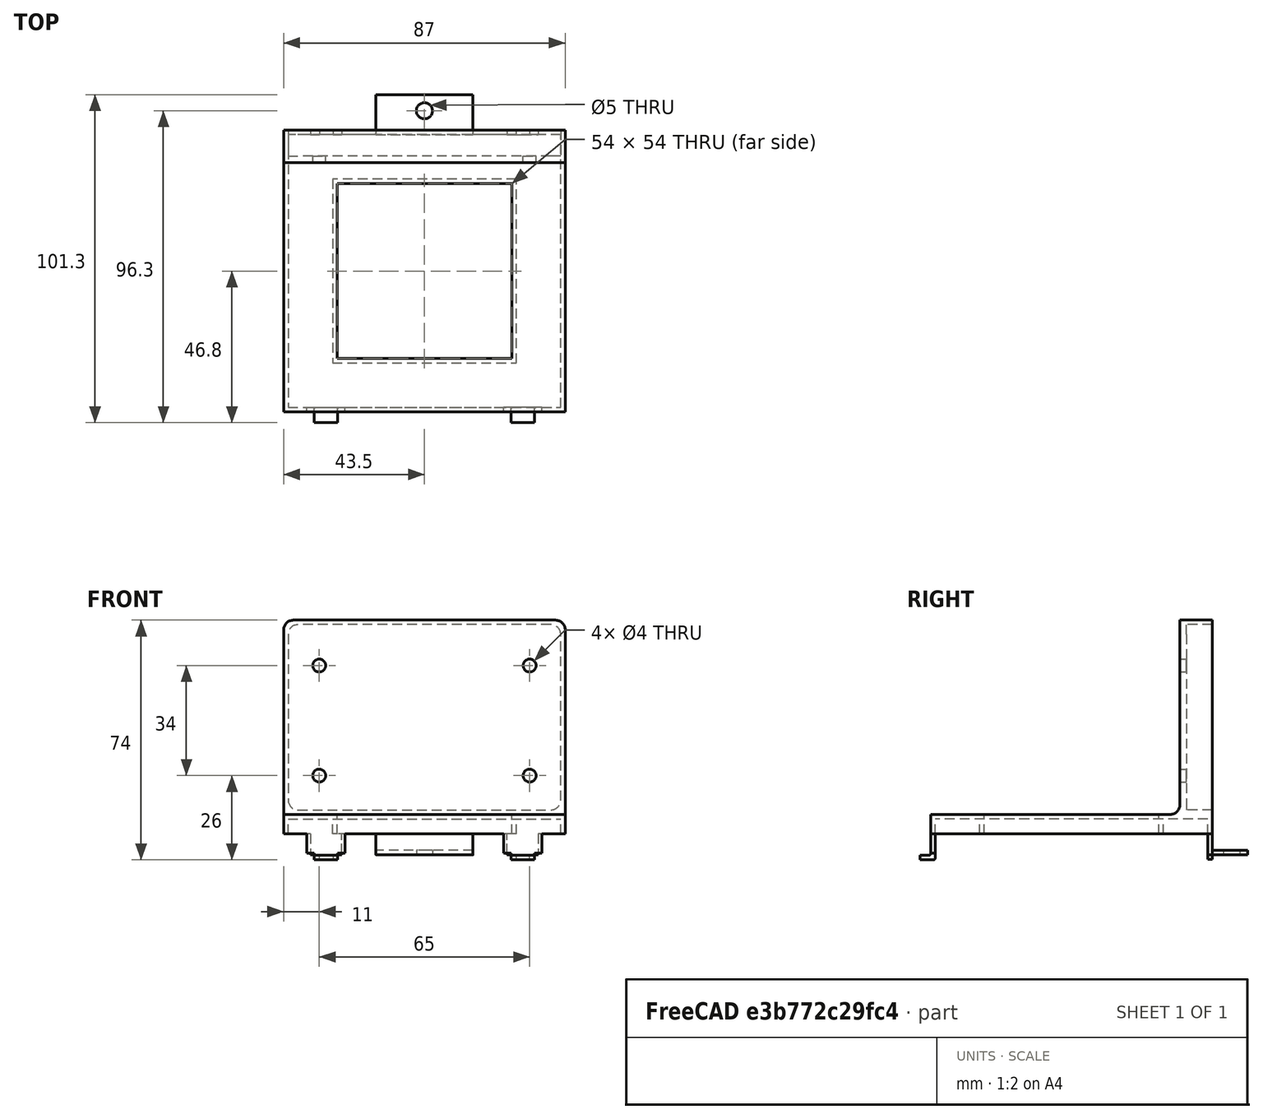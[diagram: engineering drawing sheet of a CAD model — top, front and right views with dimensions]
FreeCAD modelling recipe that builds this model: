
FCSTD DOCUMENT  (FreeCAD 0.21R33668 +7 (Git))
Label: TheTower900Adapter
License: All rights reserved
LicenseURL: http://austrianinstruments.at/All_rights_reserved
objects: TechDraw::DrawViewDimension×24, Sketcher::SketchObject×11, PartDesign::Pad×7, PartDesign::Plane×3, TechDraw::DrawProjGroupItem×3, PartDesign::Pocket×2, TechDraw::DrawSVGTemplate×2, PartDesign::Hole×2, PartDesign::Fillet×2, TechDraw::DrawPage×2, Spreadsheet::Sheet×1, TechDraw::DrawViewSymbol×1, PartDesign::Mirrored×1, PartDesign::Body×1, TechDraw::DrawProjGroup×1, TechDraw::DrawViewDetail×1, TechDraw::DrawViewPart×1
note: 50 computed .brp shape members not serialized (recipe doc carries the construction recipe); baked Part::Feature solids carry a one-line shape summary decoded from their .brp

FEATURE [Sketcher::SketchObject] Sketch
  FullyConstrained = true
  MapMode = 5
  Support = -> [XY_Plane]
  expr: Constraints[20] = Spreadsheet.mainbodywidth
  expr: Constraints[21] = Spreadsheet.mainbodyholewidth
  sketch-geometry (10):
    g0: LineSegment StartX=-43.5 StartY=43.5 StartZ=0 EndX=-43.5 EndY=-43.5 EndZ=0
    g1: LineSegment StartX=-43.5 StartY=-43.5 StartZ=0 EndX=43.5 EndY=-43.5 EndZ=0
    g2: LineSegment StartX=43.5 StartY=-43.5 StartZ=0 EndX=43.5 EndY=43.5 EndZ=0
    g3: LineSegment StartX=43.5 StartY=43.5 StartZ=0 EndX=-43.5 EndY=43.5 EndZ=0
    g4: GeomPoint X=0 Y=0 Z=0
    g5: LineSegment StartX=-27 StartY=27 StartZ=0 EndX=-27 EndY=-27 EndZ=0
    g6: LineSegment StartX=-27 StartY=-27 StartZ=0 EndX=27 EndY=-27 EndZ=0
    g7: LineSegment StartX=27 StartY=-27 StartZ=0 EndX=27 EndY=27 EndZ=0
    g8: LineSegment StartX=27 StartY=27 StartZ=0 EndX=-27 EndY=27 EndZ=0
    g9: GeomPoint X=0 Y=0 Z=0
  constraints (24):
    c: Coincident(g0,g1)
    c: Coincident(g1,g2)
    c: Coincident(g2,g3)
    c: Coincident(g3,g0)
    c: Horizontal(g1)
    c: Horizontal(g3)
    c: Vertical(g0)
    c: Vertical(g2)
    c: Symmetric(g1,g0,g4)
    c: Coincident(g4,g-1)
    c: Coincident(g5,g6)
    c: Coincident(g6,g7)
    c: Coincident(g7,g8)
    c: Coincident(g8,g5)
    c: Horizontal(g6)
    c: Horizontal(g8)
    c: Vertical(g5)
    c: Vertical(g7)
    c: Symmetric(g6,g5,g9)
    c: Coincident(g9,g4)
    c: DistanceY(g0,g0) = 87
    c: DistanceY(g5,g5) = 54
    c: Equal(g8,g5)
    c: Equal(g3,g0)
FEATURE [PartDesign::Pad] Pad  label="Main body"
  Direction = (0,0,1)
  Length = 6
  Length2 = 10
  Profile = -> Sketch
  ReferenceAxis = -> Sketch [N_Axis]
  Type = 0
  expr: Length = Spreadsheet.mainbodyheight
FEATURE [Sketcher::SketchObject] Sketch001
  FullyConstrained = true
  MapMode = 5
  Support = -> [XY_Plane]
  expr: Constraints[11] = Spreadsheet.mainbodywidth - Spreadsheet.mainbodywallthickness * 2
  expr: Constraints[22] = Spreadsheet.mainbodyholewidth + Spreadsheet.mainbodywallthickness * 2
  sketch-geometry (10):
    g0: LineSegment StartX=-42.1 StartY=42.1 StartZ=0 EndX=-42.1 EndY=-42.1 EndZ=0
    g1: LineSegment StartX=-42.1 StartY=-42.1 StartZ=0 EndX=42.1 EndY=-42.1 EndZ=0
    g2: LineSegment StartX=42.1 StartY=-42.1 StartZ=0 EndX=42.1 EndY=42.1 EndZ=0
    g3: LineSegment StartX=42.1 StartY=42.1 StartZ=0 EndX=-42.1 EndY=42.1 EndZ=0
    g4: GeomPoint X=0 Y=0 Z=0
    g5: LineSegment StartX=-28.4 StartY=28.4 StartZ=0 EndX=-28.4 EndY=-28.4 EndZ=0
    g6: LineSegment StartX=-28.4 StartY=-28.4 StartZ=0 EndX=28.4 EndY=-28.4 EndZ=0
    g7: LineSegment StartX=28.4 StartY=-28.4 StartZ=0 EndX=28.4 EndY=28.4 EndZ=0
    g8: LineSegment StartX=28.4 StartY=28.4 StartZ=0 EndX=-28.4 EndY=28.4 EndZ=0
    g9: GeomPoint X=0 Y=0 Z=0
  constraints (24):
    c: Coincident(g0,g1)
    c: Coincident(g1,g2)
    c: Coincident(g2,g3)
    c: Coincident(g3,g0)
    c: Horizontal(g1)
    c: Horizontal(g3)
    c: Vertical(g0)
    c: Vertical(g2)
    c: Symmetric(g1,g0,g4)
    c: Coincident(g4,g-1)
    c: Equal(g3,g2)
    c: DistanceY(g0,g0) = 84.2
    c: Coincident(g5,g6)
    c: Coincident(g6,g7)
    c: Coincident(g7,g8)
    c: Coincident(g8,g5)
    c: Horizontal(g6)
    c: Horizontal(g8)
    c: Vertical(g5)
    c: Vertical(g7)
    c: Symmetric(g6,g5,g9)
    c: Coincident(g9,g4)
    c: DistanceY(g5,g5) = 56.8
    c: Equal(g5,g8)
FEATURE [PartDesign::Pocket] Pocket  label="Main body pocket"
  BaseFeature = -> Pad
  Direction = (0,0,-1)
  Length = 4.6
  Length2 = 5
  Profile = -> Sketch001
  ReferenceAxis = -> Sketch001 [N_Axis]
  Reversed = true
  Type = 0
  expr: Length = Spreadsheet.mainbodypocketdepth
FEATURE [PartDesign::Plane] DatumPlane  label="Front fixture reference plane"
  AttachmentOffset = pos=(0,0,43.5) rot=(0,0,1;0rad)
  Length = 60
  MapMode = 3
  Placement = pos=(0,-43.5,9.7e-15) rot=(1,0,0;1.5708rad)
  ResizeMode = 0
  Support = -> [XY_Plane]
  Width = 60
  expr: .AttachmentOffset.Base.z = Spreadsheet.mainbodywidth / 2
FEATURE [Sketcher::SketchObject] Sketch002
  FullyConstrained = true
  MapMode = 5
  Placement = pos=(0,-43.5,9.7e-15) rot=(1,0,0;1.5708rad)
  Support = -> [DatumPlane]
  expr: Constraints[18] = Spreadsheet.frontfixturewidth1
  expr: Constraints[19] = Spreadsheet.frontfixtureheight1
  expr: Constraints[21] = Spreadsheet.frontfixturewidth2
  expr: Constraints[22] = Spreadsheet.frontfixturedistance / 2
  expr: Constraints[23] = Spreadsheet.frontfixtureheight2
  sketch-geometry (8):
    g0: LineSegment StartX=-36.3 StartY=0 StartZ=0 EndX=-24.5 EndY=0 EndZ=0
    g1: LineSegment StartX=-24.5 StartY=0 StartZ=0 EndX=-24.5 EndY=-6 EndZ=0
    g2: LineSegment StartX=-36.3 StartY=-6 StartZ=0 EndX=-36.3 EndY=0 EndZ=0
    g3: LineSegment StartX=-36.3 StartY=-6 StartZ=0 EndX=-34.025 EndY=-6 EndZ=0
    g4: LineSegment StartX=-34.025 StartY=-6 StartZ=0 EndX=-34.025 EndY=-8 EndZ=0
    g5: LineSegment StartX=-34.025 StartY=-8 StartZ=0 EndX=-26.775 EndY=-8 EndZ=0
    g6: LineSegment StartX=-26.775 StartY=-8 StartZ=0 EndX=-26.775 EndY=-6 EndZ=0
    g7: LineSegment StartX=-26.775 StartY=-6 StartZ=0 EndX=-24.5 EndY=-6 EndZ=0
  constraints (24):
    c: Coincident(g0,g1)
    c: Coincident(g2,g0)
    c: Horizontal(g0)
    c: Vertical(g1)
    c: Vertical(g2)
    c: PointOnObject(g0,g-1)
    c: Coincident(g3,g2)
    c: Horizontal(g3)
    c: Coincident(g4,g3)
    c: Vertical(g4)
    c: Coincident(g5,g4)
    c: Horizontal(g5)
    c: Coincident(g6,g5)
    c: Vertical(g6)
    c: Coincident(g7,g6)
    c: Coincident(g7,g1)
    c: Horizontal(g7)
    c: Equal(g3,g7)
    c: DistanceX(g0,g0) = 11.8
    c: DistanceY(g2,g2) = 6
    c: Horizontal(g3,g6)
    c: DistanceX(g5,g5) = 7.25
    c: DistanceX(g0,g-1) = 24.5
    c: DistanceY(g4,g2) = 2
FEATURE [PartDesign::Pad] Pad001  label="Front fixture vertical part"
  BaseFeature = -> Pocket
  Direction = (0,-1,2e-16)
  Length = 1.4
  Length2 = 10
  Profile = -> Sketch002
  ReferenceAxis = -> Sketch002 [N_Axis]
  Reversed = true
  Type = 0
  expr: Length = Spreadsheet.mainbodywallthickness
FEATURE [Sketcher::SketchObject] Sketch003
  FullyConstrained = true
  MapMode = 5
  Placement = pos=(0,-43.5,9.7e-15) rot=(1,0,0;1.5708rad)
  Support = -> [DatumPlane]
  expr: Constraints[10] = Spreadsheet.frontfixturedistance / 2 + (Spreadsheet.frontfixturewidth1 - Spreadsheet.frontfixturewidth2) / 2
  expr: Constraints[11] = Spreadsheet.frontfixtureheight1 + Spreadsheet.frontfixtureheight2
  expr: Constraints[7] = Spreadsheet.mainbodywallthickness
  expr: Constraints[9] = Spreadsheet.frontfixturewidth2
  sketch-geometry (4):
    g0: LineSegment StartX=-34.025 StartY=-6.6 StartZ=0 EndX=-26.775 EndY=-6.6 EndZ=0
    g1: LineSegment StartX=-26.775 StartY=-6.6 StartZ=0 EndX=-26.775 EndY=-8 EndZ=0
    g2: LineSegment StartX=-26.775 StartY=-8 StartZ=0 EndX=-34.025 EndY=-8 EndZ=0
    g3: LineSegment StartX=-34.025 StartY=-8 StartZ=0 EndX=-34.025 EndY=-6.6 EndZ=0
  constraints (12):
    c: Horizontal(g0)
    c: Vertical(g1)
    c: Vertical(g3)
    c: Coincident(g1,g2)
    c: Coincident(g2,g3)
    c: Coincident(g0,g3)
    c: Coincident(g0,g1)
    c: DistanceY(g3,g3) = 1.4
    c: Horizontal(g2)
    c: DistanceX(g0,g0) = 7.25
    c: DistanceX(g0,g-1) = 26.775
    c: DistanceY(g1,g-1) = 8
FEATURE [PartDesign::Pad] Pad002  label="Front fixture horizontal part"
  BaseFeature = -> Pad001
  Direction = (0,-1,2e-16)
  Length = 3.3
  Length2 = 10
  Profile = -> Sketch003
  ReferenceAxis = -> Sketch003 [N_Axis]
  Type = 0
  expr: Length = Spreadsheet.frontfixturehorizontalpartlength
FEATURE [Spreadsheet::Sheet] Spreadsheet
  cells = A1='mainbodywidth; B1(mainbodywidth)=87; A2='mainbodyholewidth; B2(mainbodyholewidth)=54; A3='mainbodyheight; B3(mainbodyheight)=6; A4='mainbodywallthickness; B4(mainbodywallthickness)=1.4; A5='mainbodypocketdepth; B5(mainbodypocketdepth)==mainbodyheight - mainbodywallthickness; A6='frontfixturedistance; B6(frontfixturedistance)=49; A7='frontfixturewidth1; B7(frontfixturewidth1)=11.8; A8='frontfixturewidth2; B8(frontfixturewidth2)=7.25; A9='frontfixtureheight1; B9(frontfixtureheight1)==12 - mainbodyheight; A10='frontfixtureheight2; B10(frontfixtureheight2)==14 - mainbodyheight - frontfixtureheight1; A11='frontfixturehorizontalpartlength; B11(frontfixturehorizontalpartlength)=3.3; A12='backfixturedistance; B12(backfixturedistance)=51; A13='backfixturewidth1; B13(backfixturewidth1)=9.7; A14='backfixturewidth2; B14(backfixturewidth2)=4.2; A15='backfixtureheight1; B15(backfixtureheight1)==12.5 - mainbodyheight; A16='backfixtureheight2; B16(backfixtureheight2)==13.85 - backfixtureheight1 - mainbodyheight; A17='floorfixtureverticalwidth; B17(floorfixtureverticalwidth)=30; A18='floorfixturehorizontalpartheight; B18(floorfixturehorizontalpartheight)==mainbodywallthickness; A19='floorfixturehorizontalparthlength; B19(floorfixturehorizontalparthlength)=11; A20='socketlength; B20(socketlength)=10; A21='socketheight; B21(socketheight)=60; A22='socketholeshorizontaldistance; B22(socketholeshorizontaldistance)=65; A23='socketholesverticaldistance; B23(socketholesverticaldistance)=34; A24='socketholescenterheight; B24(socketholescenterheight)=35; A25='socketholesradius; B25(socketholesradius)=2
FEATURE [PartDesign::Plane] DatumPlane001  label="Back fixture reference plane"
  AttachmentOffset = pos=(0,0,-43.5) rot=(0,0,1;0rad)
  Length = 60
  MapMode = 5
  Placement = pos=(0,43.5,9.7e-15) rot=(1,0,0;1.5708rad)
  ResizeMode = 0
  Support = -> [XZ_Plane]
  Width = 60
  expr: .AttachmentOffset.Base.z = -Spreadsheet.mainbodywidth / 2
FEATURE [Sketcher::SketchObject] Sketch004
  FullyConstrained = true
  MapMode = 5
  Placement = pos=(0,43.5,9.7e-15) rot=(1,0,0;1.5708rad)
  Support = -> [DatumPlane001]
  expr: Constraints[10] = Spreadsheet.backfixtureheight1
  expr: Constraints[8] = Spreadsheet.floorfixtureverticalwidth
  sketch-geometry (4):
    g0: LineSegment StartX=-15 StartY=0 StartZ=0 EndX=15 EndY=0 EndZ=0
    g1: LineSegment StartX=15 StartY=0 StartZ=0 EndX=15 EndY=-6.5 EndZ=0
    g2: LineSegment StartX=15 StartY=-6.5 StartZ=0 EndX=-15 EndY=-6.5 EndZ=0
    g3: LineSegment StartX=-15 StartY=-6.5 StartZ=0 EndX=-15 EndY=0 EndZ=0
  constraints (11):
    c: Coincident(g0,g1)
    c: Coincident(g1,g2)
    c: Coincident(g2,g3)
    c: Coincident(g3,g0)
    c: Horizontal(g0)
    c: Horizontal(g2)
    c: Vertical(g1)
    c: Vertical(g3)
    c: DistanceX(g2,g2) = 30
    c: Symmetric(g0,g0,g-1)
    c: DistanceY(g3,g3) = 6.5
FEATURE [PartDesign::Plane] DatumPlane002  label="top reference plane"
  AttachmentOffset = pos=(0,0,6) rot=(0,0,1;0rad)
  Length = 60
  MapMode = 5
  Placement = pos=(0,0,6) rot=(0,0,1;0rad)
  ResizeMode = 0
  Support = -> [XY_Plane]
  Width = 60
FEATURE [Sketcher::SketchObject] Sketch006
  FullyConstrained = true
  MapMode = 5
  Placement = pos=(0,0,6) rot=(0,0,1;0rad)
  Support = -> [DatumPlane002]
  expr: Constraints[10] = Spreadsheet.mainbodywidth
  expr: Constraints[11] = Spreadsheet.mainbodywidth / 2
  expr: Constraints[12] = Spreadsheet.socketlength
  sketch-geometry (5):
    g0: LineSegment StartX=-43.5 StartY=43.5 StartZ=0 EndX=-43.5 EndY=33.5 EndZ=0
    g1: LineSegment StartX=-43.5 StartY=33.5 StartZ=0 EndX=43.5 EndY=33.5 EndZ=0
    g2: LineSegment StartX=43.5 StartY=33.5 StartZ=0 EndX=43.5 EndY=43.5 EndZ=0
    g3: LineSegment StartX=43.5 StartY=43.5 StartZ=0 EndX=-43.5 EndY=43.5 EndZ=0
    g4: GeomPoint X=0 Y=38.5 Z=0
  constraints (13):
    c: Coincident(g0,g1)
    c: Coincident(g1,g2)
    c: Coincident(g2,g3)
    c: Coincident(g3,g0)
    c: Horizontal(g1)
    c: Horizontal(g3)
    c: Vertical(g0)
    c: Vertical(g2)
    c: Symmetric(g1,g0,g4)
    c: PointOnObject(g4,g-2)
    c: DistanceX(g3,g3) = 87
    c: DistanceY(g-1,g0) = 43.5
    c: DistanceY(g0,g0) = 10
FEATURE [Sketcher::SketchObject] Sketch007
  FullyConstrained = true
  MapMode = 5
  Placement = pos=(0,0,0) rot=(1,0,0;1.5708rad)
  Support = -> [XZ_Plane]
  expr: Constraints[12] = Spreadsheet.socketholescenterheight
  expr: Constraints[7] = Spreadsheet.socketholesradius
  expr: Constraints[8] = Spreadsheet.socketholeshorizontaldistance
  expr: Constraints[9] = Spreadsheet.socketholesverticaldistance
  sketch-geometry (5):
    g0: Circle CenterX=-32.5 CenterY=52 CenterZ=0 NormalX=0 NormalY=0 NormalZ=1 AngleXU=0 Radius=2
    g1: Circle CenterX=32.5 CenterY=52 CenterZ=0 NormalX=0 NormalY=0 NormalZ=1 AngleXU=0 Radius=2
    g2: Circle CenterX=-32.5 CenterY=18 CenterZ=0 NormalX=0 NormalY=0 NormalZ=1 AngleXU=0 Radius=2
    g3: Circle CenterX=32.5 CenterY=18 CenterZ=0 NormalX=0 NormalY=0 NormalZ=1 AngleXU=0 Radius=2
    g4: GeomPoint X=0 Y=35 Z=0
  constraints (13):
    c: Vertical(g1,g3)
    c: Vertical(g0,g2)
    c: Horizontal(g0,g1)
    c: Horizontal(g2,g3)
    c: Equal(g0,g1)
    c: Equal(g1,g3)
    c: Equal(g3,g2)
    c: Radius(g0) = 2
    c: DistanceX(g0,g1) = 65
    c: DistanceY(g2,g0) = 34
    c: PointOnObject(g4,g-2)
    c: Symmetric(g0,g3,g4)
    c: DistanceY(g-1,g4) = 35
FEATURE [Sketcher::SketchObject] Sketch005
  FullyConstrained = true
  MapMode = 5
  Placement = pos=(0,43.5,9.7e-15) rot=(1,0,0;1.5708rad)
  Support = -> [DatumPlane001]
  expr: Constraints[10] = Spreadsheet.floorfixtureverticalwidth
  expr: Constraints[11] = Spreadsheet.backfixtureheight1
  expr: Constraints[12] = Spreadsheet.mainbodywallthickness
  sketch-geometry (5):
    g0: LineSegment StartX=-15 StartY=-5.1 StartZ=0 EndX=-15 EndY=-6.5 EndZ=0
    g1: LineSegment StartX=-15 StartY=-6.5 StartZ=0 EndX=15 EndY=-6.5 EndZ=0
    g2: LineSegment StartX=15 StartY=-6.5 StartZ=0 EndX=15 EndY=-5.1 EndZ=0
    g3: LineSegment StartX=15 StartY=-5.1 StartZ=0 EndX=-15 EndY=-5.1 EndZ=0
    g4: GeomPoint X=0 Y=-5.8 Z=0
  constraints (13):
    c: Coincident(g0,g1)
    c: Coincident(g1,g2)
    c: Coincident(g2,g3)
    c: Coincident(g3,g0)
    c: Horizontal(g1)
    c: Horizontal(g3)
    c: Vertical(g0)
    c: Vertical(g2)
    c: Symmetric(g1,g0,g4)
    c: PointOnObject(g4,g-2)
    c: DistanceX(g1,g1) = 30
    c: DistanceY(g0,g-1) = 6.5
    c: DistanceY(g0,g0) = 1.4
FEATURE [Sketcher::SketchObject] Sketch008
  FullyConstrained = true
  MapMode = 5
  Support = -> [XY_Plane]
  expr: Constraints[2] = Spreadsheet.mainbodywidth / 2 + Spreadsheet.floorfixturehorizontalparthlength - 5
  sketch-geometry (1):
    g0: Circle CenterX=0 CenterY=49.5 CenterZ=0 NormalX=0 NormalY=0 NormalZ=1 AngleXU=0 Radius=2.5
  constraints (3):
    c: PointOnObject(g0,g-2)
    c: Radius(g0) = 2.5
    c: DistanceY(g-1,g0) = 49.5
FEATURE [Sketcher::SketchObject] Sketch009
  FullyConstrained = true
  MapMode = 5
  Placement = pos=(0,43.5,9.7e-15) rot=(1,0,0;1.5708rad)
  Support = -> [DatumPlane001]
  expr: Constraints[10] = Spreadsheet.mainbodyheight + Spreadsheet.socketheight / 2
  expr: Constraints[11] = Spreadsheet.mainbodywidth - Spreadsheet.mainbodywallthickness * 2
  expr: Constraints[12] = Spreadsheet.socketheight - Spreadsheet.mainbodywallthickness * 2
  sketch-geometry (5):
    g0: LineSegment StartX=-42.1 StartY=64.6 StartZ=0 EndX=-42.1 EndY=7.4 EndZ=0
    g1: LineSegment StartX=-42.1 StartY=7.4 StartZ=0 EndX=42.1 EndY=7.4 EndZ=0
    g2: LineSegment StartX=42.1 StartY=7.4 StartZ=0 EndX=42.1 EndY=64.6 EndZ=0
    g3: LineSegment StartX=42.1 StartY=64.6 StartZ=0 EndX=-42.1 EndY=64.6 EndZ=0
    g4: GeomPoint X=1e-16 Y=36 Z=0
  constraints (13):
    c: Coincident(g0,g1)
    c: Coincident(g1,g2)
    c: Coincident(g2,g3)
    c: Coincident(g3,g0)
    c: Horizontal(g1)
    c: Horizontal(g3)
    c: Vertical(g0)
    c: Vertical(g2)
    c: Symmetric(g1,g0,g4)
    c: PointOnObject(g4,g-2)
    c: DistanceY(g-1,g4) = 36
    c: DistanceX(g3,g3) = 84.2
    c: DistanceY(g2,g2) = 57.2
FEATURE [TechDraw::DrawSVGTemplate] Template
  EditableTexts = APPROVER_NAME=Equilibrium; AUTHOR_NAME=Equilibrium; DATE=2023-09-01; DN=1; DOCUMENT_TYPE=Mechanical assembly drawing; OWNER_NAME=Equilibrium; PM=Plastic; PN=1; REVISION=REV 1; RIGHTS=Can be distributed without permission; SCALE=M x:x; SHEET=1 of 1; SIZE=A3; TITLELINE-1=Adapter for PC Waterpump; TITLELINE-2=EK-Quantum Kinetic TBE 300 D5 PWM D-RGB; TITLELINE-3=for The Tower 900 Chassis; TOLERANCE=+/- ?
  Height = 297
  Orientation = 1
  Width = 420
FEATURE [TechDraw::DrawSVGTemplate] Template001
  EditableTexts = APPROVER_NAME=Equilibrium; AUTHOR_NAME=Equilibrium; DATE=2023-09-01; DN=1; DOCUMENT_TYPE=Mechanical assembly drawing; OWNER_NAME=Equilibrium; PM=Plastic; PN=1; REVISION=REV 1; RIGHTS=(R) DO NOT DUPLICATE THIS DRAWING TO THIRD PARTIES WITHOUT OWNER'S PERMISSION!; SCALE=M x:x; SHEET=1 of 1; SIZE=A3; TITLELINE-1=Adapter for PC Waterpump; TITLELINE-2=EK-Quantum Kinetic TBE 300 D5 PWM D-RGB; TITLELINE-3=for The Tower 900 Chassis; TOLERANCE=+/- ?
  Height = 297
  Orientation = 1
  Width = 420
FEATURE [TechDraw::DrawViewSymbol] SurfaceSymbol
  LockPosition = false
  Rotation = 0
  ScaleType = 2
  Symbol = <?xml version='1.0'?>\n<svg width='150' height='64'>\n<path stroke='#000' stroke-width='1' d=' M0, 44 L12, 64' />\n<path stroke='#000' stroke-width='1' d=' M12, 64 L42, 14' />\n<circle cx='12' cy='46' r='9' fill='none' stroke='#000' stroke-width='1'/>\n<text x='42' y='11' style='font-size:18px'>3D Print</text>\n<text x='42' y='30' style='font-size:18px'>Ra50</text>\n<path stroke='#000' stroke-width='1' d=' M42, 14 L116, 14' />\n<text x='20' y='60' style='font-size:18px'></text>\n<text x='-25' y='60' style='font-size:18px'></text>\n</svg>
  X = 155
  Y = 275.5
FEATURE [Sketcher::SketchObject] Sketch010
  FullyConstrained = true
  MapMode = 5
  Placement = pos=(0,43.5,9.7e-15) rot=(1,0,0;1.5708rad)
  Support = -> [DatumPlane001]
  expr: Constraints[20] = Spreadsheet.backfixturewidth2
  expr: Constraints[21] = Spreadsheet.backfixturedistance / 2
  expr: Constraints[22] = Spreadsheet.backfixtureheight1
  expr: Constraints[23] = Spreadsheet.backfixtureheight2
  expr: Constraints[9] = Spreadsheet.backfixturewidth1
  sketch-geometry (8):
    g0: LineSegment StartX=-25.5 StartY=0 StartZ=0 EndX=-35.2 EndY=0 EndZ=0
    g1: LineSegment StartX=-35.2 StartY=0 StartZ=0 EndX=-35.2 EndY=-6.5 EndZ=0
    g2: LineSegment StartX=-35.2 StartY=-6.5 StartZ=0 EndX=-32.45 EndY=-6.5 EndZ=0
    g3: LineSegment StartX=-25.5 StartY=-6.5 StartZ=0 EndX=-25.5 EndY=0 EndZ=0
    g4: LineSegment StartX=-28.25 StartY=-6.5 StartZ=0 EndX=-28.25 EndY=-7.85 EndZ=0
    g5: LineSegment StartX=-28.25 StartY=-7.85 StartZ=0 EndX=-32.45 EndY=-7.85 EndZ=0
    g6: LineSegment StartX=-32.45 StartY=-7.85 StartZ=0 EndX=-32.45 EndY=-6.5 EndZ=0
    g7: LineSegment StartX=-28.25 StartY=-6.5 StartZ=0 EndX=-25.5 EndY=-6.5 EndZ=0
  constraints (24):
    c: Coincident(g0,g1)
    c: Coincident(g1,g2)
    c: Coincident(g7,g3)
    c: Coincident(g3,g0)
    c: Horizontal(g0)
    c: Horizontal(g2)
    c: Vertical(g1)
    c: Vertical(g3)
    c: PointOnObject(g0,g-1)
    c: DistanceX(g0,g0) = 9.7
    c: Coincident(g5,g4)
    c: Horizontal(g5)
    c: Coincident(g6,g5)
    c: Coincident(g2,g6)
    c: Coincident(g7,g4)
    c: Equal(g7,g2)
    c: Equal(g3,g1)
    c: Vertical(g4)
    c: Vertical(g6)
    c: Horizontal(g7)
    c: DistanceX(g5,g5) = 4.2
    c: DistanceX(g0,g-1) = 25.5
    c: DistanceY(g1,g1) = 6.5
    c: DistanceY(g5,g1) = 1.35
FEATURE [PartDesign::Pad] Pad006  label="Back fixture vertical part"
  BaseFeature = -> Pad002
  Direction = (0,-1,-2e-16)
  Length = 1.4
  Length2 = 10
  Profile = -> Sketch010
  ReferenceAxis = -> Sketch010 [N_Axis]
  Type = 0
  expr: Length = Spreadsheet.mainbodywallthickness
FEATURE [PartDesign::Mirrored] Mirrored002  label="Fixture mirroring"
  BaseFeature = -> Pad006
  MirrorPlane = -> Sketch003 [V_Axis]
  Originals = -> [Pad001,Pad002,Pad006]
FEATURE [PartDesign::Pad] Pad003  label="Floor fixture vertical"
  BaseFeature = -> Mirrored002
  Direction = (0,-1,-2e-16)
  Length = 1.4
  Length2 = 10
  Profile = -> Sketch004
  ReferenceAxis = -> Sketch004 [N_Axis]
  Type = 0
  expr: Length = Spreadsheet.mainbodywallthickness
FEATURE [PartDesign::Pad] Pad004  label="Floor fixture horizontal"
  BaseFeature = -> Pad003
  Direction = (0,-1,-2e-16)
  Length = 11
  Length2 = 10
  Profile = -> Sketch005
  ReferenceAxis = -> Sketch005 [N_Axis]
  Reversed = true
  Type = 0
  expr: Length = Spreadsheet.floorfixturehorizontalparthlength
FEATURE [PartDesign::Hole] Hole001  label="Floow fixture hole"
  BaseFeature = -> Pad004
  CustomThreadClearance = 0
  Depth = 305.896
  DepthType = 1
  Diameter = 5
  DrillForDepth = false
  DrillPoint = 1
  DrillPointAngle = 118
  HoleCutCountersinkAngle = 90
  HoleCutCustomValues = false
  HoleCutDepth = 0
  HoleCutDiameter = 6.1
  HoleCutType = 0
  ModelThread = false
  Profile = -> Sketch008
  Tapered = false
  TaperedAngle = 90
  ThreadClass = 0
  ThreadDepth = 305.896
  ThreadDepthType = 0
  ThreadDirection = 0
  ThreadFit = 0
  ThreadSize = 0
  ThreadType = 0
  Threaded = false
  UseCustomThreadClearance = false
FEATURE [PartDesign::Pad] Pad005  label="Socket"
  BaseFeature = -> Hole001
  Direction = (0,0,1)
  Length = 60
  Length2 = 10
  Profile = -> Sketch006
  ReferenceAxis = -> Sketch006 [N_Axis]
  Type = 0
  expr: Length = Spreadsheet.socketheight
FEATURE [PartDesign::Hole] Hole  label="Socket holes"
  BaseFeature = -> Pad005
  CustomThreadClearance = 0
  Depth = 305.896
  DepthType = 1
  Diameter = 4
  DrillForDepth = false
  DrillPoint = 1
  DrillPointAngle = 118
  HoleCutCountersinkAngle = 90
  HoleCutCustomValues = false
  HoleCutDepth = 0
  HoleCutDiameter = 6.1
  HoleCutType = 0
  ModelThread = false
  Profile = -> Sketch007
  Tapered = false
  TaperedAngle = 90
  ThreadClass = 0
  ThreadDepth = 305.896
  ThreadDepthType = 0
  ThreadDirection = 0
  ThreadFit = 0
  ThreadSize = 0
  ThreadType = 0
  Threaded = false
  UseCustomThreadClearance = false
FEATURE [PartDesign::Pocket] Pocket001  label="Socket pocket"
  BaseFeature = -> Hole
  Direction = (0,1,2e-16)
  Length = 8
  Length2 = 5
  Profile = -> Sketch009
  ReferenceAxis = -> Sketch009 [N_Axis]
  Reversed = true
  Type = 0
FEATURE [PartDesign::Fillet] Fillet  label="Fillet 3mm"
  Base = -> Pocket001 [Edge105,Edge102,Edge223,Edge228,Edge226,Edge224,Edge71]
  BaseFeature = -> Pocket001
  Radius = 3
  SupportTransform = false
  UseAllEdges = false
FEATURE [PartDesign::Fillet] Fillet001  label="Fillet 0.5mm"
  Base = -> Fillet [Edge123,Edge212,Edge85,Edge75,Edge218,Edge219]
  BaseFeature = -> Fillet
  Radius = 0.5
  SupportTransform = false
  UseAllEdges = false
FEATURE [PartDesign::Body] Body
  Chassis = https://de.thermaltake.com/the-tower-900.html
  Group = -> [Sketch,Pad,Sketch001,Pocket,DatumPlane,DatumPlane001,Sketch002,Pad001,Sketch003,Pad002,Pad006,Mirrored002,Sketch004,Pad003,Sketch005,Pad004,DatumPlane002,Hole001,Sketch006,Pad005,Sketch007,Hole,Sketch008,Sketch009,Pocket001,Fillet,Fillet001,Sketch010]
  Origin = -> Origin
  Tip = -> Fillet001
  Waterpump = https://www.ekwb.com/shop/ek-quantum-kinetic-tbe-300-d5-pwm-d-rgb-acetal
FEATURE [TechDraw::DrawProjGroupItem] ProjItem  label="Front"
  CoarseView = false
  Direction = (-9e-16,-1,0)
  Focus = 100
  HardHidden = false
  IsoCount = 0
  IsoHidden = false
  IsoVisible = false
  LockPosition = true
  Perspective = false
  Rotation = 0
  RotationVector = (1,0,0)
  ScaleType = 2
  ScrubCount = 0
  SeamHidden = false
  SeamVisible = true
  SmoothHidden = false
  SmoothVisible = true
  Source = -> [Body]
  Type = 0
  X = 0
  XDirection = (1,-9e-16,0)
  Y = 0
FEATURE [TechDraw::DrawProjGroupItem] ProjItem002  label="Left"
  CoarseView = false
  Direction = (-1,8e-16,0)
  Focus = 100
  HardHidden = false
  IsoCount = 0
  IsoHidden = false
  IsoVisible = false
  LockPosition = false
  Perspective = false
  Rotation = 0
  RotationVector = (1,0,0)
  ScaleType = 2
  ScrubCount = 0
  SeamHidden = false
  SeamVisible = true
  SmoothHidden = false
  SmoothVisible = true
  Source = -> [Body]
  Type = 1
  X = 154.15
  XDirection = (-8e-16,-1,0)
  Y = 0
FEATURE [TechDraw::DrawProjGroupItem] ProjItem003  label="Top"
  CoarseView = false
  Direction = (0,0,1)
  Focus = 100
  HardHidden = false
  IsoCount = 0
  IsoHidden = false
  IsoVisible = false
  LockPosition = false
  Perspective = false
  Rotation = 0
  RotationVector = (1,0,0)
  ScaleType = 2
  ScrubCount = 0
  SeamHidden = false
  SeamVisible = true
  SmoothHidden = false
  SmoothVisible = true
  Source = -> [Body]
  Type = 4
  X = 0
  XDirection = (1,-9e-16,0)
  Y = -127.65
FEATURE [TechDraw::DrawProjGroup] ProjGroup
  Anchor = -> ProjItem
  AutoDistribute = true
  LockPosition = false
  ProjectionType = 0
  Rotation = 0
  Scale = 0.75
  ScaleType = 0
  Source = -> [Body]
  Views = -> [ProjItem,ProjItem002,ProjItem003]
  X = 100
  Y = 230
  spacingX = 60
  spacingY = 40
FEATURE [TechDraw::DrawViewDimension] Dimension
  AngleOverride = false
  Arbitrary = false
  ArbitraryTolerances = false
  EqualTolerance = true
  ExtensionAngle = 0
  FormatSpec = %.2w
  FormatSpecOverTolerance = %+.2w
  FormatSpecUnderTolerance = %+.2w
  Inverted = false
  LineAngle = 0
  LockPosition = false
  MeasureType = 1
  OverTolerance = 0
  References2D = -> [ProjItem003]
  Rotation = 0
  ScaleType = 0
  TheoreticalExact = false
  Type = 1
  UnderTolerance = 0
  X = 2.25574
  Y = -61.5796
FEATURE [TechDraw::DrawViewDimension] Dimension001
  AngleOverride = false
  Arbitrary = false
  ArbitraryTolerances = false
  EqualTolerance = true
  ExtensionAngle = 0
  FormatSpec = %.2w
  FormatSpecOverTolerance = %+.2w
  FormatSpecUnderTolerance = %+.2w
  Inverted = false
  LineAngle = 0
  LockPosition = false
  MeasureType = 1
  OverTolerance = 0
  References2D = -> [ProjItem003]
  Rotation = 0
  ScaleType = 0
  TheoreticalExact = false
  Type = 2
  UnderTolerance = 0
  X = 67.9134
  Y = -1.35
FEATURE [TechDraw::DrawViewDimension] Dimension002
  AngleOverride = false
  Arbitrary = false
  ArbitraryTolerances = false
  EqualTolerance = true
  ExtensionAngle = 0
  FormatSpec = %.2w
  FormatSpecOverTolerance = %+.2w
  FormatSpecUnderTolerance = %+.2w
  Inverted = false
  LineAngle = 0
  LockPosition = false
  MeasureType = 1
  OverTolerance = 0
  References2D = -> [ProjItem003]
  Rotation = 0
  ScaleType = 0
  TheoreticalExact = false
  Type = 2
  UnderTolerance = 0
  X = 55.077
  Y = 48.6162
FEATURE [TechDraw::DrawViewDimension] Dimension003
  AngleOverride = false
  Arbitrary = false
  ArbitraryTolerances = false
  EqualTolerance = true
  ExtensionAngle = 0
  FormatSpec = %.2w
  FormatSpecOverTolerance = %+.2w
  FormatSpecUnderTolerance = %+.2w
  Inverted = false
  LineAngle = 0
  LockPosition = false
  MeasureType = 1
  OverTolerance = 0
  References2D = -> [ProjItem003]
  Rotation = 0
  ScaleType = 0
  TheoreticalExact = false
  Type = 2
  UnderTolerance = 0
  X = 61.1392
  Y = -1.35
FEATURE [TechDraw::DrawViewDimension] Dimension004
  AngleOverride = false
  Arbitrary = false
  ArbitraryTolerances = false
  EqualTolerance = true
  ExtensionAngle = 0
  FormatSpec = %.2w
  FormatSpecOverTolerance = %+.2w
  FormatSpecUnderTolerance = %+.2w
  Inverted = false
  LineAngle = 0
  LockPosition = false
  MeasureType = 1
  OverTolerance = 0
  References2D = -> [ProjItem003]
  Rotation = 0
  ScaleType = 0
  TheoreticalExact = false
  Type = 1
  UnderTolerance = 0
  X = 1.74054
  Y = -54.2162
FEATURE [TechDraw::DrawViewDimension] Dimension005
  AngleOverride = false
  Arbitrary = false
  ArbitraryTolerances = false
  EqualTolerance = true
  ExtensionAngle = 0
  FormatSpec = %.2w
  FormatSpecOverTolerance = %+.2w
  FormatSpecUnderTolerance = %+.2w
  Inverted = false
  LineAngle = 0
  LockPosition = false
  MeasureType = 1
  OverTolerance = 0
  References2D = -> [ProjItem003]
  Rotation = 0
  ScaleType = 0
  TheoreticalExact = false
  Type = 1
  UnderTolerance = 0
  X = 0.454091
  Y = 64.1901
FEATURE [TechDraw::DrawViewDimension] Dimension006
  AngleOverride = false
  Arbitrary = false
  ArbitraryTolerances = false
  EqualTolerance = true
  ExtensionAngle = 0
  FormatSpec = %.2w
  FormatSpecOverTolerance = %+.2w
  FormatSpecUnderTolerance = %+.2w
  Inverted = false
  LineAngle = 0
  LockPosition = false
  MeasureType = 1
  OverTolerance = 0
  References2D = -> [ProjItem003]
  Rotation = 0
  ScaleType = 0
  TheoreticalExact = false
  Type = 2
  UnderTolerance = 0
  X = -49.1786
  Y = 61.4903
FEATURE [TechDraw::DrawViewDimension] Dimension008
  AngleOverride = false
  Arbitrary = false
  ArbitraryTolerances = false
  EqualTolerance = true
  ExtensionAngle = 0
  FormatSpec = %.2w
  FormatSpecOverTolerance = %+.2w
  FormatSpecUnderTolerance = %+.2w
  Inverted = false
  LineAngle = 0
  LockPosition = false
  MeasureType = 1
  OverTolerance = 0
  References2D = -> [ProjItem002]
  Rotation = 0
  ScaleType = 0
  TheoreticalExact = false
  Type = 2
  UnderTolerance = 0
  X = -61.1579
  Y = -1.19603
FEATURE [TechDraw::DrawViewDimension] Dimension009
  AngleOverride = false
  Arbitrary = false
  ArbitraryTolerances = false
  EqualTolerance = true
  ExtensionAngle = 0
  FormatSpec = %.2w
  FormatSpecOverTolerance = %+.2w
  FormatSpecUnderTolerance = %+.2w
  Inverted = false
  LineAngle = 0
  LockPosition = false
  MeasureType = 1
  OverTolerance = 0
  References2D = -> [ProjItem002]
  Rotation = 0
  ScaleType = 0
  TheoreticalExact = false
  Type = 2
  UnderTolerance = 0
  X = -70.6178
  Y = -1.30714
FEATURE [TechDraw::DrawViewDimension] Dimension011
  AngleOverride = false
  Arbitrary = false
  ArbitraryTolerances = false
  EqualTolerance = true
  ExtensionAngle = 0
  FormatSpec = %.2w
  FormatSpecOverTolerance = %+.2w
  FormatSpecUnderTolerance = %+.2w
  Inverted = false
  LineAngle = 0
  LockPosition = false
  MeasureType = 1
  OverTolerance = 0
  References2D = -> [ProjItem002]
  Rotation = 0
  ScaleType = 0
  TheoreticalExact = false
  Type = 1
  UnderTolerance = 0
  X = -32.4637
  Y = -41.0217
FEATURE [TechDraw::DrawViewDimension] Dimension012
  AngleOverride = false
  Arbitrary = false
  ArbitraryTolerances = false
  EqualTolerance = true
  ExtensionAngle = 0
  FormatSpec = %.2w
  FormatSpecOverTolerance = %+.2w
  FormatSpecUnderTolerance = %+.2w
  Inverted = false
  LineAngle = 0
  LockPosition = false
  MeasureType = 1
  OverTolerance = 0
  References2D = -> [ProjItem002]
  Rotation = 0
  ScaleType = 0
  TheoreticalExact = false
  Type = 1
  UnderTolerance = 0
  X = 37.9895
  Y = -41.0132
FEATURE [TechDraw::DrawViewDimension] Dimension013
  AngleOverride = false
  Arbitrary = false
  ArbitraryTolerances = false
  EqualTolerance = true
  ExtensionAngle = 0
  FormatSpec = %.2w
  FormatSpecOverTolerance = %+.2w
  FormatSpecUnderTolerance = %+.2w
  Inverted = false
  LineAngle = 0
  LockPosition = false
  MeasureType = 1
  OverTolerance = 0
  References2D = -> [ProjItem002]
  Rotation = 0
  ScaleType = 0
  TheoreticalExact = false
  Type = 2
  UnderTolerance = 0
  X = 57.6209
  Y = -26.9967
FEATURE [TechDraw::DrawViewDimension] Dimension014
  AngleOverride = false
  Arbitrary = false
  ArbitraryTolerances = false
  EqualTolerance = true
  ExtensionAngle = 0
  FormatSpec = %.2w
  FormatSpecOverTolerance = %+.2w
  FormatSpecUnderTolerance = %+.2w
  Inverted = false
  LineAngle = 0
  LockPosition = false
  MeasureType = 1
  OverTolerance = 0
  References2D = -> [ProjItem002]
  Rotation = 0
  ScaleType = 0
  TheoreticalExact = false
  Type = 2
  UnderTolerance = 0
  X = 49.1463
  Y = -14.7359
FEATURE [TechDraw::DrawViewDetail] Detail  label="Detail Fixture"
  AnchorPoint = (30.45,-32.71,0)
  BaseView = -> ProjItem
  Caption = Detail 1
  CoarseView = false
  Direction = (-9e-16,-1,0)
  Focus = 100
  HardHidden = false
  IsoCount = 0
  IsoHidden = false
  IsoVisible = false
  LockPosition = true
  Perspective = false
  Radius = 10
  Reference = 1
  Rotation = 0
  Scale = 3
  ScaleType = 2
  ScrubCount = 0
  SeamHidden = false
  SeamVisible = true
  SmoothHidden = false
  SmoothVisible = true
  Source = -> [Body]
  X = 240
  XDirection = (1,-9e-16,0)
  Y = 130
FEATURE [TechDraw::DrawViewDimension] Dimension018
  AngleOverride = false
  Arbitrary = false
  ArbitraryTolerances = false
  EqualTolerance = true
  ExtensionAngle = 0
  FormatSpec = %.2w
  FormatSpecOverTolerance = %+.2w
  FormatSpecUnderTolerance = %+.2w
  Inverted = false
  LineAngle = 0
  LockPosition = false
  MeasureType = 1
  OverTolerance = 0
  References2D = -> [Detail]
  Rotation = 0
  ScaleType = 0
  TheoreticalExact = false
  Type = 2
  UnderTolerance = 0
  X = 22.2258
  Y = 4.25735
FEATURE [TechDraw::DrawViewDimension] Dimension019
  AngleOverride = false
  Arbitrary = false
  ArbitraryTolerances = false
  EqualTolerance = true
  ExtensionAngle = 0
  FormatSpec = %.2w
  FormatSpecOverTolerance = %+.2w
  FormatSpecUnderTolerance = %+.2w
  Inverted = false
  LineAngle = 0
  LockPosition = false
  MeasureType = 1
  OverTolerance = 0
  References2D = -> [Detail]
  Rotation = 0
  ScaleType = 0
  TheoreticalExact = false
  Type = 2
  UnderTolerance = 0
  X = 36.2258
  Y = 1.25735
FEATURE [TechDraw::DrawViewDimension] Dimension020
  AngleOverride = false
  Arbitrary = false
  ArbitraryTolerances = false
  EqualTolerance = true
  ExtensionAngle = 0
  FormatSpec = %.2w
  FormatSpecOverTolerance = %+.2w
  FormatSpecUnderTolerance = %+.2w
  Inverted = false
  LineAngle = 0
  LockPosition = false
  MeasureType = 1
  OverTolerance = 0
  References2D = -> [Detail]
  Rotation = 0
  ScaleType = 0
  TheoreticalExact = false
  Type = 2
  UnderTolerance = 0
  X = 29.2258
  Y = 2.75735
FEATURE [TechDraw::DrawViewDimension] Dimension021
  AngleOverride = false
  Arbitrary = false
  ArbitraryTolerances = false
  EqualTolerance = true
  ExtensionAngle = 0
  FormatSpec = %.2w
  FormatSpecOverTolerance = %+.2w
  FormatSpecUnderTolerance = %+.2w
  Inverted = false
  LineAngle = 0
  LockPosition = false
  MeasureType = 1
  OverTolerance = 0
  References2D = -> [Detail]
  Rotation = 0
  ScaleType = 0
  TheoreticalExact = false
  Type = 1
  UnderTolerance = 0
  X = 0.525
  Y = -23.2252
FEATURE [TechDraw::DrawViewDimension] Dimension022
  AngleOverride = false
  Arbitrary = false
  ArbitraryTolerances = false
  EqualTolerance = true
  ExtensionAngle = 0
  FormatSpec = %.2w
  FormatSpecOverTolerance = %+.2w
  FormatSpecUnderTolerance = %+.2w
  Inverted = false
  LineAngle = 0
  LockPosition = false
  MeasureType = 1
  OverTolerance = 0
  References2D = -> [Detail]
  Rotation = 0
  ScaleType = 0
  TheoreticalExact = false
  Type = 1
  UnderTolerance = 0
  X = 0.525
  Y = -16.2252
FEATURE [TechDraw::DrawViewDimension] Dimension023
  AngleOverride = false
  Arbitrary = false
  ArbitraryTolerances = false
  EqualTolerance = true
  ExtensionAngle = 0
  FormatSpec = %.2w
  FormatSpecOverTolerance = %+.2w
  FormatSpecUnderTolerance = %+.2w
  Inverted = false
  LineAngle = 0
  LockPosition = false
  MeasureType = 1
  OverTolerance = 0
  References2D = -> [ProjItem]
  Rotation = 0
  ScaleType = 0
  TheoreticalExact = false
  Type = 2
  UnderTolerance = 0
  X = -24.8831
  Y = -47.3633
FEATURE [TechDraw::DrawViewDimension] Dimension024
  AngleOverride = false
  Arbitrary = false
  ArbitraryTolerances = false
  EqualTolerance = true
  ExtensionAngle = 0
  FormatSpec = %.2w
  FormatSpecOverTolerance = %+.2w
  FormatSpecUnderTolerance = %+.2w
  Inverted = false
  LineAngle = 0
  LockPosition = false
  MeasureType = 1
  OverTolerance = 0
  References2D = -> [ProjItem002]
  Rotation = 0
  ScaleType = 0
  TheoreticalExact = false
  Type = 2
  UnderTolerance = 0
  X = -49.7184
  Y = 7.90996
FEATURE [TechDraw::DrawViewPart] View
  CoarseView = false
  Direction = (0.386,-0.831,0.401)
  Focus = 100
  HardHidden = false
  IsoCount = 0
  IsoHidden = false
  IsoVisible = false
  LockPosition = false
  Perspective = false
  Rotation = 0
  Scale = 2
  ScaleType = 0
  ScrubCount = 0
  SeamHidden = false
  SeamVisible = true
  SmoothHidden = false
  SmoothVisible = true
  Source = -> [Body]
  X = 210
  XDirection = (0.907,0.422,0)
  Y = 148.5
FEATURE [TechDraw::DrawPage] Page001  label="3D View"
  KeepUpdated = true
  NextBalloonIndex = 1
  ProjectionType = 0
  Scale = 2
  Template = -> Template001
  Views = -> [View]
FEATURE [TechDraw::DrawViewDimension] Dimension026
  AngleOverride = false
  Arbitrary = false
  ArbitraryTolerances = false
  EqualTolerance = true
  ExtensionAngle = 0
  FormatSpec = %.2w
  FormatSpecOverTolerance = %+.2w
  FormatSpecUnderTolerance = %+.2w
  Inverted = false
  LineAngle = 0
  LockPosition = false
  MeasureType = 1
  OverTolerance = 0
  References2D = -> [ProjItem]
  Rotation = 0
  ScaleType = 0
  TheoreticalExact = false
  Type = 1
  UnderTolerance = 0
  X = 1.1892
  Y = 50.7705
FEATURE [TechDraw::DrawViewDimension] Dimension027
  AngleOverride = false
  Arbitrary = false
  ArbitraryTolerances = false
  EqualTolerance = true
  ExtensionAngle = 0
  FormatSpec = %.2w
  FormatSpecOverTolerance = %+.2w
  FormatSpecUnderTolerance = %+.2w
  Inverted = false
  LineAngle = 0
  LockPosition = false
  MeasureType = 1
  OverTolerance = 0
  References2D = -> [ProjItem]
  Rotation = 0
  ScaleType = 0
  TheoreticalExact = false
  Type = 2
  UnderTolerance = 0
  X = -58.2165
  Y = 8.05405
FEATURE [TechDraw::DrawViewDimension] Dimension028
  AngleOverride = false
  Arbitrary = false
  ArbitraryTolerances = false
  EqualTolerance = true
  ExtensionAngle = 0
  FormatSpec = %.2w
  FormatSpecOverTolerance = %+.2w
  FormatSpecUnderTolerance = %+.2w
  Inverted = false
  LineAngle = 0
  LockPosition = false
  MeasureType = 1
  OverTolerance = 0
  References2D = -> [ProjItem]
  Rotation = 0
  ScaleType = 0
  TheoreticalExact = false
  Type = 1
  UnderTolerance = 0
  X = -39.046
  Y = 50.6915
FEATURE [TechDraw::DrawViewDimension] Dimension029
  AngleOverride = false
  Arbitrary = false
  ArbitraryTolerances = false
  EqualTolerance = true
  ExtensionAngle = 0
  FormatSpec = %.2w
  FormatSpecOverTolerance = %+.2w
  FormatSpecUnderTolerance = %+.2w
  Inverted = false
  LineAngle = 0
  LockPosition = false
  MeasureType = 1
  OverTolerance = 0
  References2D = -> [ProjItem]
  Rotation = 0
  ScaleType = 0
  TheoreticalExact = false
  Type = 2
  UnderTolerance = 0
  X = -58.3396
  Y = 32.2097
FEATURE [TechDraw::DrawPage] Page  label="Technical drawing"
  KeepUpdated = true
  NextBalloonIndex = 2
  ProjectionType = 0
  Template = -> Template
  Views = -> [ProjGroup,Dimension,Dimension001,Dimension002,Dimension003,Dimension004,Dimension005,Dimension006,Dimension008,Dimension009,Dimension011,Dimension012,Dimension013,Dimension014,Detail,Dimension018,Dimension019,Dimension020,Dimension021,Dimension022,Dimension023,Dimension024,SurfaceSymbol,Dimension026,Dimension027,Dimension028,Dimension029]
